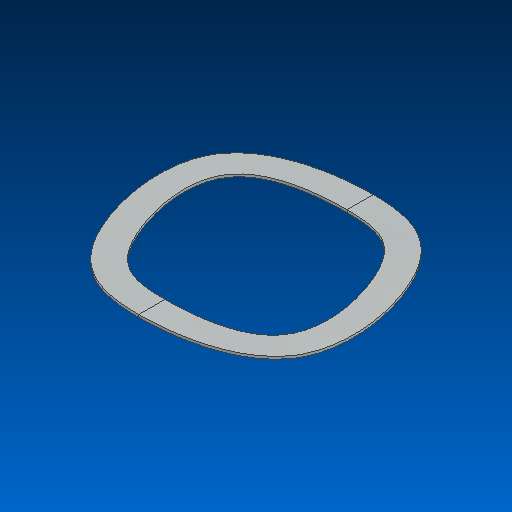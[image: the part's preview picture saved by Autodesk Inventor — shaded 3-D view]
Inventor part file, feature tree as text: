
AUTODESK INVENTOR PART (.ipt)
format: ipt  version: 2022.2 (Build 262287000, 287)  size: 125,952 bytes
history: native  units: in
note: dims shown in document units (in); Inventor stores cm internally (conversion verified against a paired STEP export)
features: loft x1
ambient origin geometry x8: Origin, YZ Plane, XZ Plane, XY Plane, X Axis, Y Axis, Z Axis, Center Point
bodies: Solid1 (feature_tree)
feature tree (1):
  loft  "Loft1"
